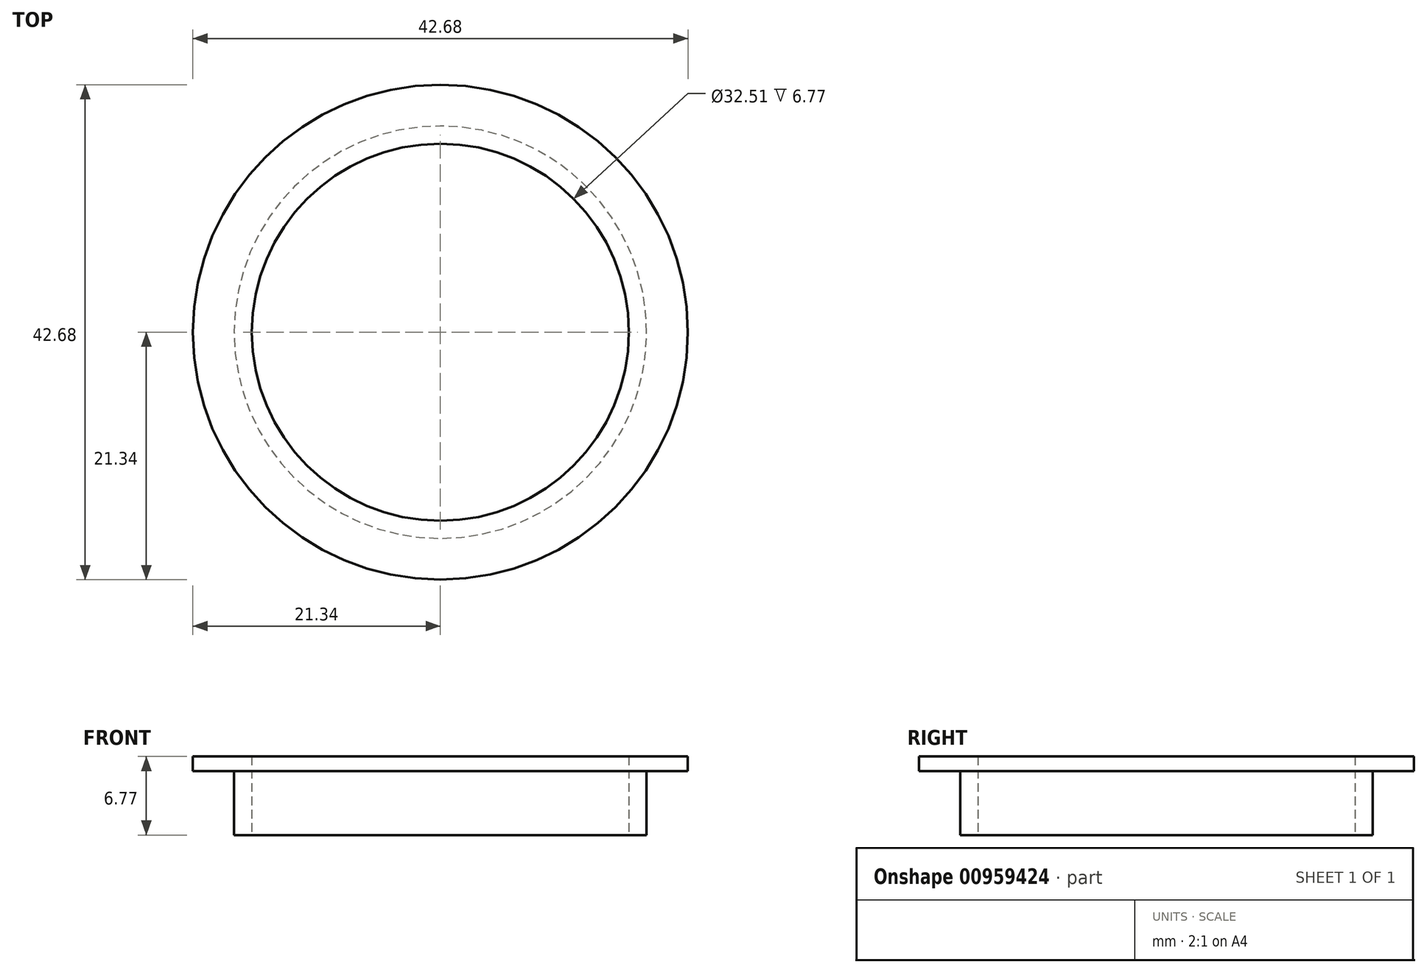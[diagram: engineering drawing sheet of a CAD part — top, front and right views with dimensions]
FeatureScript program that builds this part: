
annotation { "Feature Type Name" : "Feature", "Feature Type Description" : "" }
export const myFeature = defineFeature(function(context is Context, id is Id, definition is map)
    precondition{}
    {
        {
            var Q0;
            Q0=qCreatedBy(makeId("Front.planeOp"),FACE);
            var sketch = newSketch(context, id + "F0", { "sketchPlane" : qUnion([Q0])});
            skLineSegment(sketch, "E0", {"start": v(0, -7.94) * mm, "end": v(0, 7.13) * mm});
            skLineSegment(sketch, "E1", {"start": v(17.78, -1.8) * mm, "end": v(16.26, -1.8) * mm});
            skLineSegment(sketch, "E2", {"start": v(16.26, -1.8) * mm, "end": v(16.26, 4.97) * mm});
            skLineSegment(sketch, "E3", {"start": v(16.26, 4.97) * mm, "end": v(21.34, 4.97) * mm});
            skLineSegment(sketch, "E4", {"start": v(21.34, 4.97) * mm, "end": v(21.34, 3.7) * mm});
            skLineSegment(sketch, "E5", {"start": v(21.34, 3.7) * mm, "end": v(17.78, 3.7) * mm});
            skLineSegment(sketch, "E6", {"start": v(17.78, 3.7) * mm, "end": v(17.78, -1.8) * mm});
            skSolve(sketch);
        }
        {
            var Q0;
            Q0 = qSketchRegion(id + "F0", true);
            var Q1;
            Q1=sQuery(id+"F0.wireOp",EDGE,"E0");
            revolve(context, id + "F1", {"surfaceOperationType" : NewSurfaceOperationType.NEW, "entities" : qUnion([Q0]), "axis" : qUnion([Q1]), "revolveType" : RevolveType.FULL});
        }
    });
